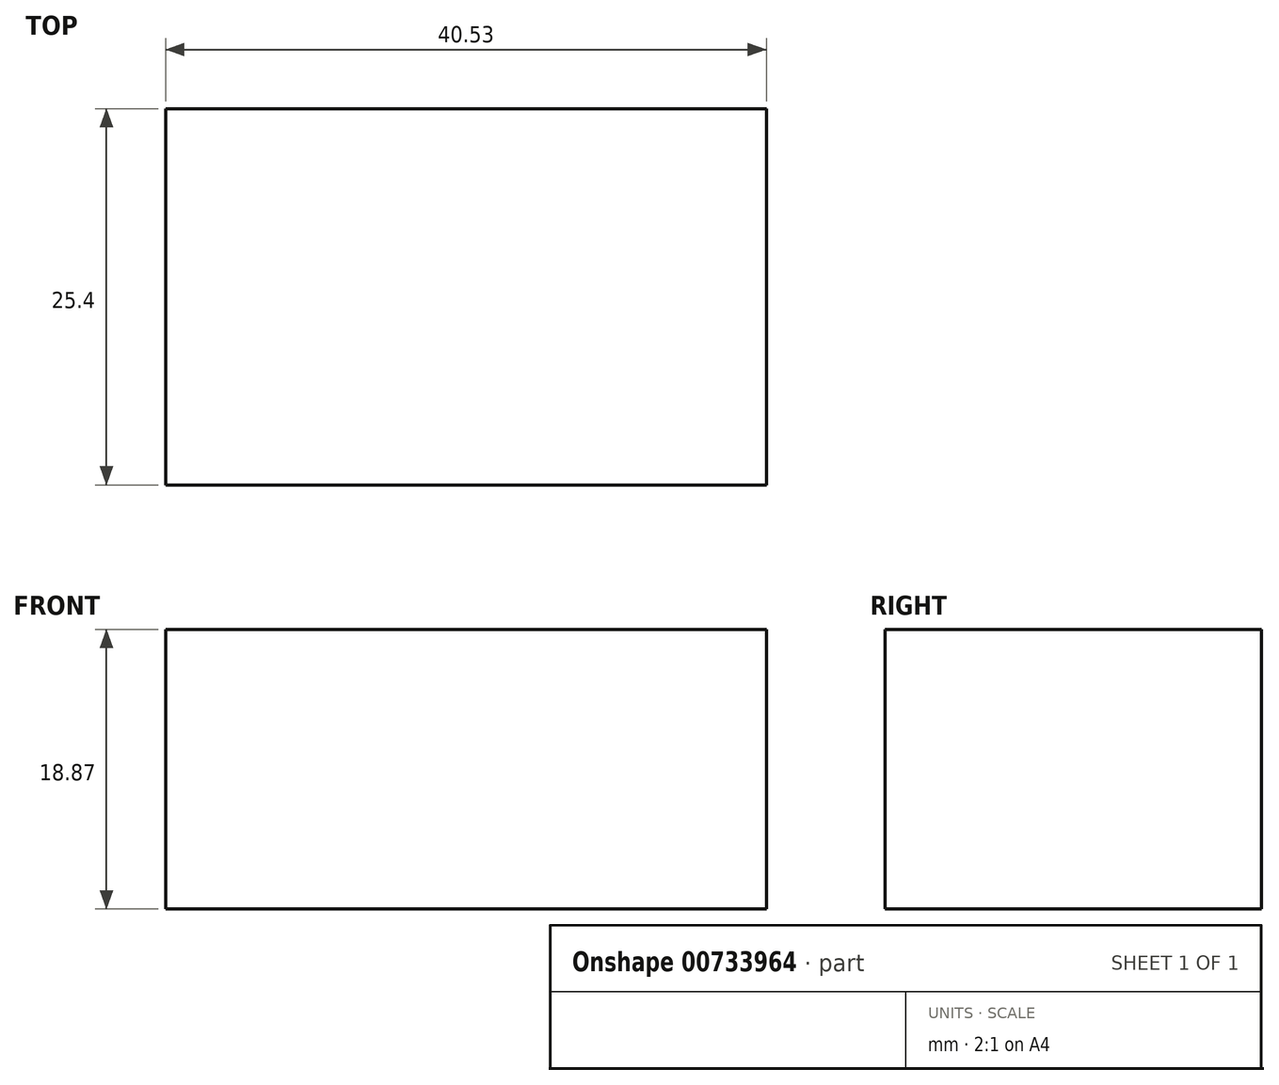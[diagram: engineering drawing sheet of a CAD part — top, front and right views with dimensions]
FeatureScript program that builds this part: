
annotation { "Feature Type Name" : "Feature", "Feature Type Description" : "" }
export const myFeature = defineFeature(function(context is Context, id is Id, definition is map)
    precondition{}
    {
        {
            var Q0;
            Q0=qCreatedBy(makeId("Front.planeOp"),FACE);
            var sketch = newSketch(context, id + "F0", { "sketchPlane" : qUnion([Q0])});
            skLineSegment(sketch, "E0.bottom", {"start": v(-49.44, 40.97) * mm, "end": v(-8.9, 40.97) * mm});
            skLineSegment(sketch, "E0.top", {"start": v(-49.44, 22.1) * mm, "end": v(-8.9, 22.1) * mm});
            skLineSegment(sketch, "E0.left", {"start": v(-49.44, 40.97) * mm, "end": v(-49.44, 22.1) * mm});
            skLineSegment(sketch, "E0.right", {"start": v(-8.9, 40.97) * mm, "end": v(-8.9, 22.1) * mm});
            skSolve(sketch);
        }
        {
            var Q0;
            Q0=makeQuery(id+"F0.imprint","IMPRINT",FACE,{"disambiguationData":[TD([[makeQuery(id+"F0.imprint","IMPRINT",EDGE,{"derivedFrom":sQuery(id+"F0.wireOp",EDGE,"E0.bottom")}),-1.0]])]});
            extrude(context, id + "F1", {"entities" : qUnion([Q0]), "depth" : 25.4 * mm, "offsetDistance" : 25.4 * mm});
        }
    });
